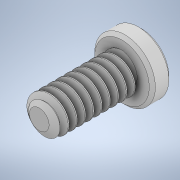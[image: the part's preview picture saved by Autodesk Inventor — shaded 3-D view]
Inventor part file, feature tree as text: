
AUTODESK INVENTOR PART (.ipt)
format: ipt  version: 2022.2 (Build 262287030, 287C)  size: 525,824 bytes
history: native  units: in
note: dims shown in document units (in); Inventor stores cm internally (conversion verified against a paired STEP export)
features: chamfer x1
ambient origin geometry x8: Origin, YZ Plane, XZ Plane, XY Plane, X Axis, Y Axis, Z Axis, Center Point
bodies: Solid1 (feature_tree)
feature tree (1):
  chamfer  "Chamfer1"  [1 undecoded]
note: 1 required parameter value undecoded (feature->parameter linkage not recoverable at this tier; creation-order binding heuristic only, values carry confidence <= 0.55)
